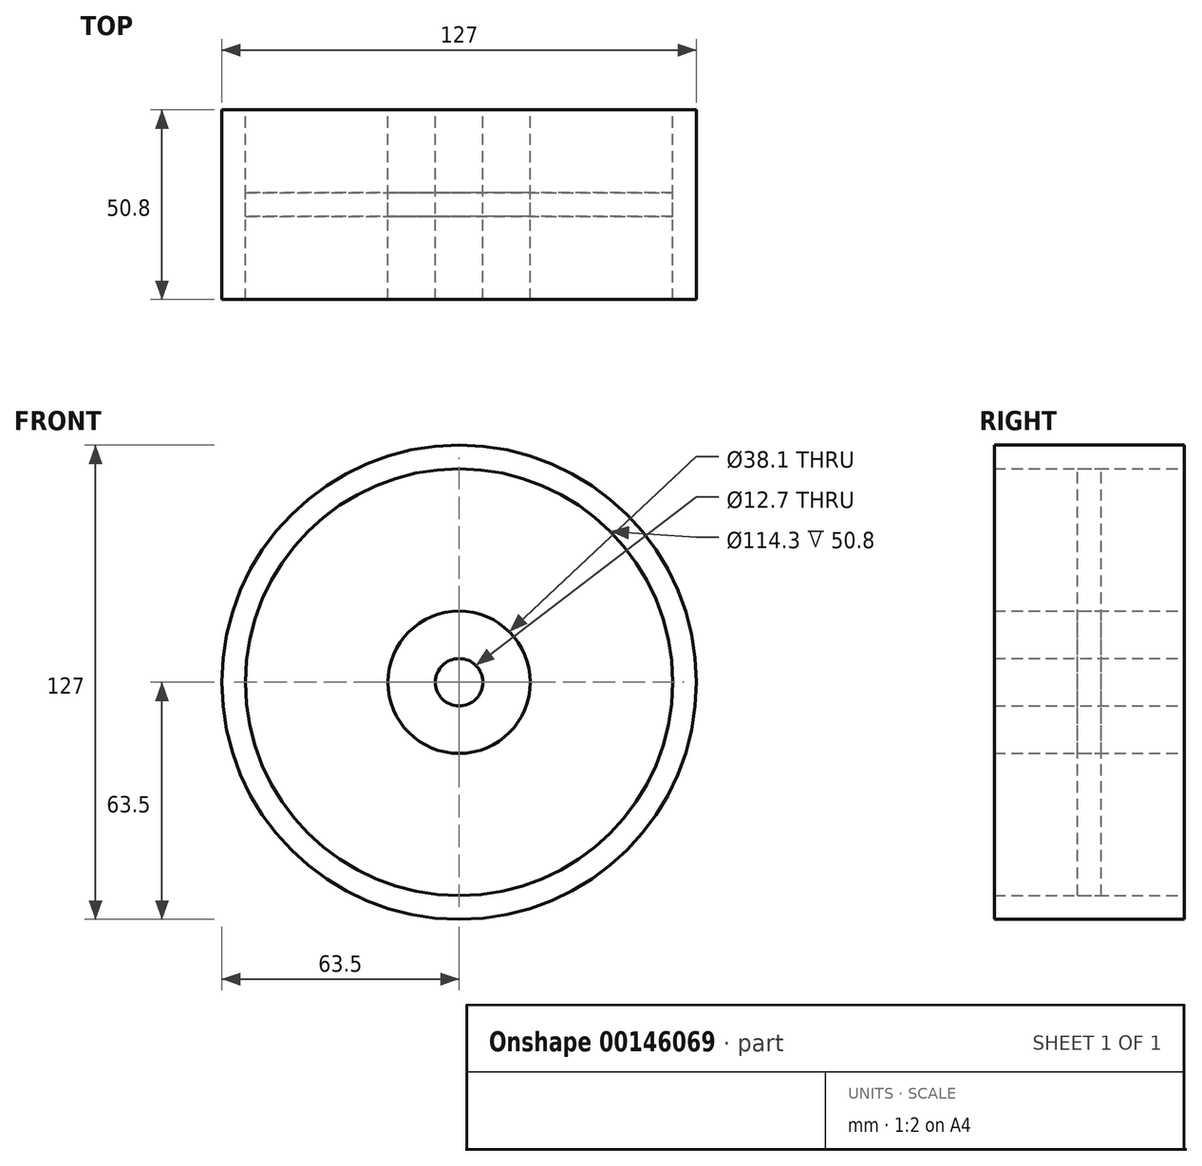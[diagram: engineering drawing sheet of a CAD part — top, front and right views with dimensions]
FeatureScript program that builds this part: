
annotation { "Feature Type Name" : "Feature", "Feature Type Description" : "" }
export const myFeature = defineFeature(function(context is Context, id is Id, definition is map)
    precondition{}
    {
        {
            var Q0;
            Q0=qCreatedBy(makeId("Front.planeOp"),FACE);
            var sketch = newSketch(context, id + "F0", { "sketchPlane" : qUnion([Q0])});
            skCircle(sketch, "E0", {"center": v(0, 0) * mm, "radius": 19.05 * mm});
            skCircle(sketch, "E1", {"center": v(0, 0) * mm, "radius": 63.5 * mm});
            skCircle(sketch, "E2", {"center": v(0, 0) * mm, "radius": 57.15 * mm});
            skCircle(sketch, "E3", {"center": v(0, 0) * mm, "radius": 6.35 * mm});
            skSolve(sketch);
        }
        {
            var Q0;
            Q0=makeQuery(id+"F0.imprint","IMPRINT",FACE,{"disambiguationData":[TD([[makeQuery(id+"F0.imprint","IMPRINT",EDGE,{"derivedFrom":sQuery(id+"F0.wireOp",EDGE,"E1")}),1.0]])]});
            var Q1;
            Q1=makeQuery(id+"F0.imprint","IMPRINT",FACE,{"disambiguationData":[TD([[makeQuery(id+"F0.imprint","IMPRINT",EDGE,{"derivedFrom":sQuery(id+"F0.wireOp",EDGE,"E0")}),1.0]])]});
            extrude(context, id + "F1", {"entities" : qUnion([Q0, Q1]), "endBound" : BoundingType.SYMMETRIC, "depth" : 50.8 * mm});
        }
        {
            var Q0;
            Q0=qCreatedBy(makeId("Front.planeOp"),FACE);
            var sketch = newSketch(context, id + "F2", { "sketchPlane" : qUnion([Q0])});
            skCircle(sketch, "E4.0", {"center": v(0, 0) * mm, "radius": 57.15 * mm});
            skCircle(sketch, "E5.0", {"center": v(0, 0) * mm, "radius": 19.05 * mm});
            skSolve(sketch);
        }
        {
            var Q0;
            Q0 = qSketchRegion(id + "F2", true);
            extrude(context, id + "F3", {"entities" : qUnion([Q0]), "endBound" : BoundingType.SYMMETRIC, "depth" : 6.35 * mm});
        }
    });
